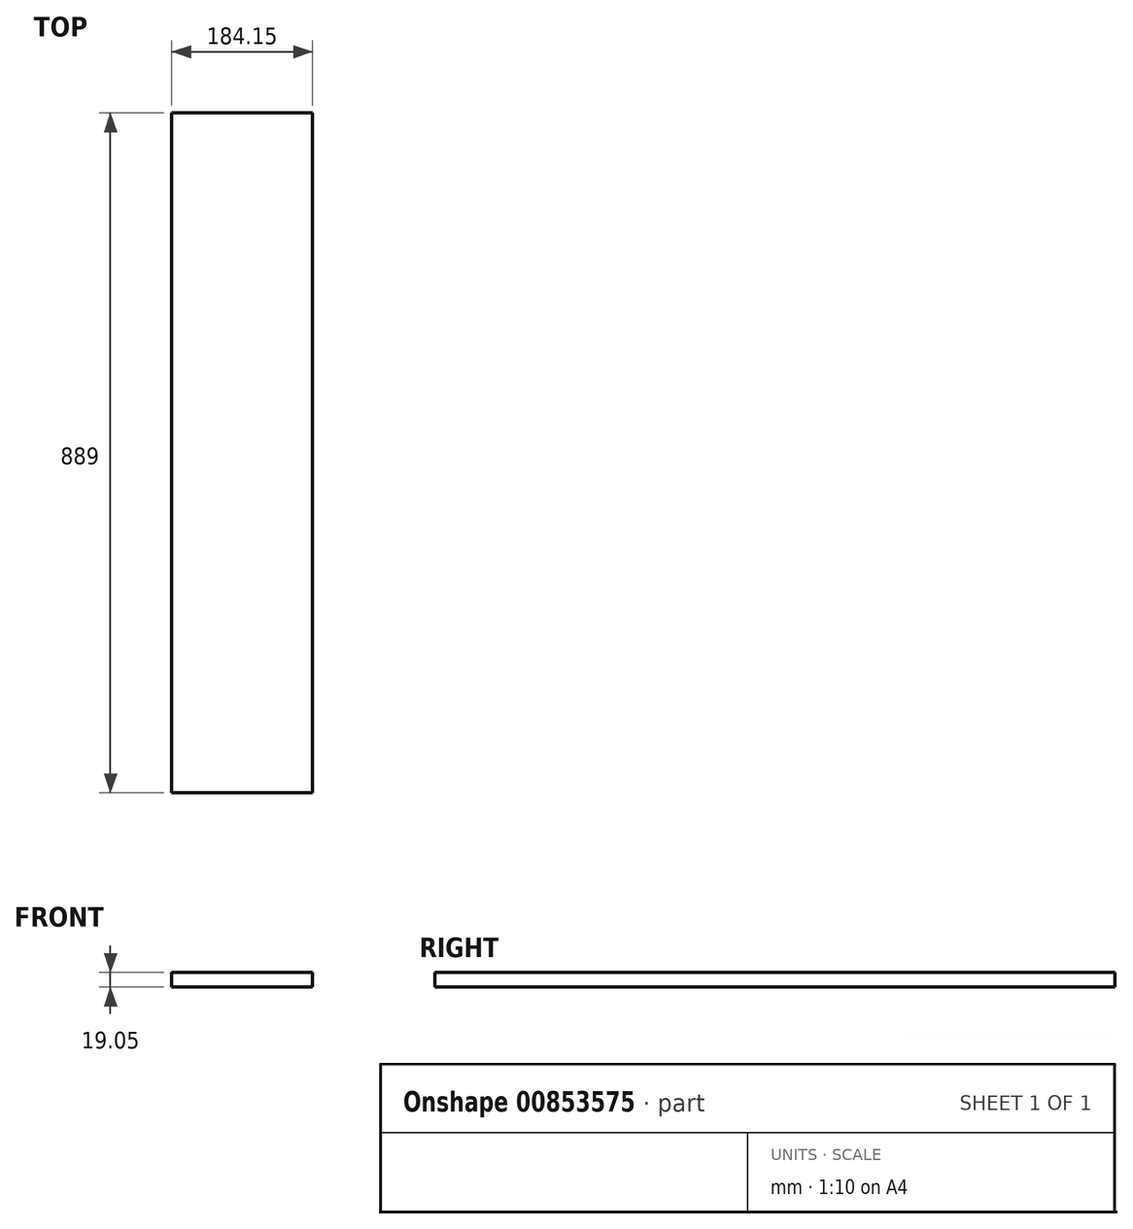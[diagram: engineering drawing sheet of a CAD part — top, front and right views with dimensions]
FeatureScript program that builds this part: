
annotation { "Feature Type Name" : "Feature", "Feature Type Description" : "" }
export const myFeature = defineFeature(function(context is Context, id is Id, definition is map)
    precondition{}
    {
        {
            var Q0;
            Q0=qCreatedBy(makeId("Front.planeOp"),FACE);
            var sketch = newSketch(context, id + "F0", { "sketchPlane" : qUnion([Q0])});
            skLineSegment(sketch, "E0.bottom", {"start": v(0, 0) * mm, "end": v(184.15, 0) * mm});
            skLineSegment(sketch, "E0.top", {"start": v(0, 19.05) * mm, "end": v(184.15, 19.05) * mm});
            skLineSegment(sketch, "E0.left", {"start": v(0, 0) * mm, "end": v(0, 19.05) * mm});
            skLineSegment(sketch, "E0.right", {"start": v(184.15, 0) * mm, "end": v(184.15, 19.05) * mm});
            skSolve(sketch);
        }
        {
            var Q0;
            Q0=makeQuery(id+"F0.imprint","IMPRINT",FACE,{"disambiguationData":[TD([[makeQuery(id+"F0.imprint","IMPRINT",EDGE,{"derivedFrom":sQuery(id+"F0.wireOp",EDGE,"E0.bottom")}),1.0]])]});
            extrude(context, id + "F1", {"entities" : qUnion([Q0]), "depth" : 889 * mm, "offsetDistance" : 25.4 * mm});
        }
    });
